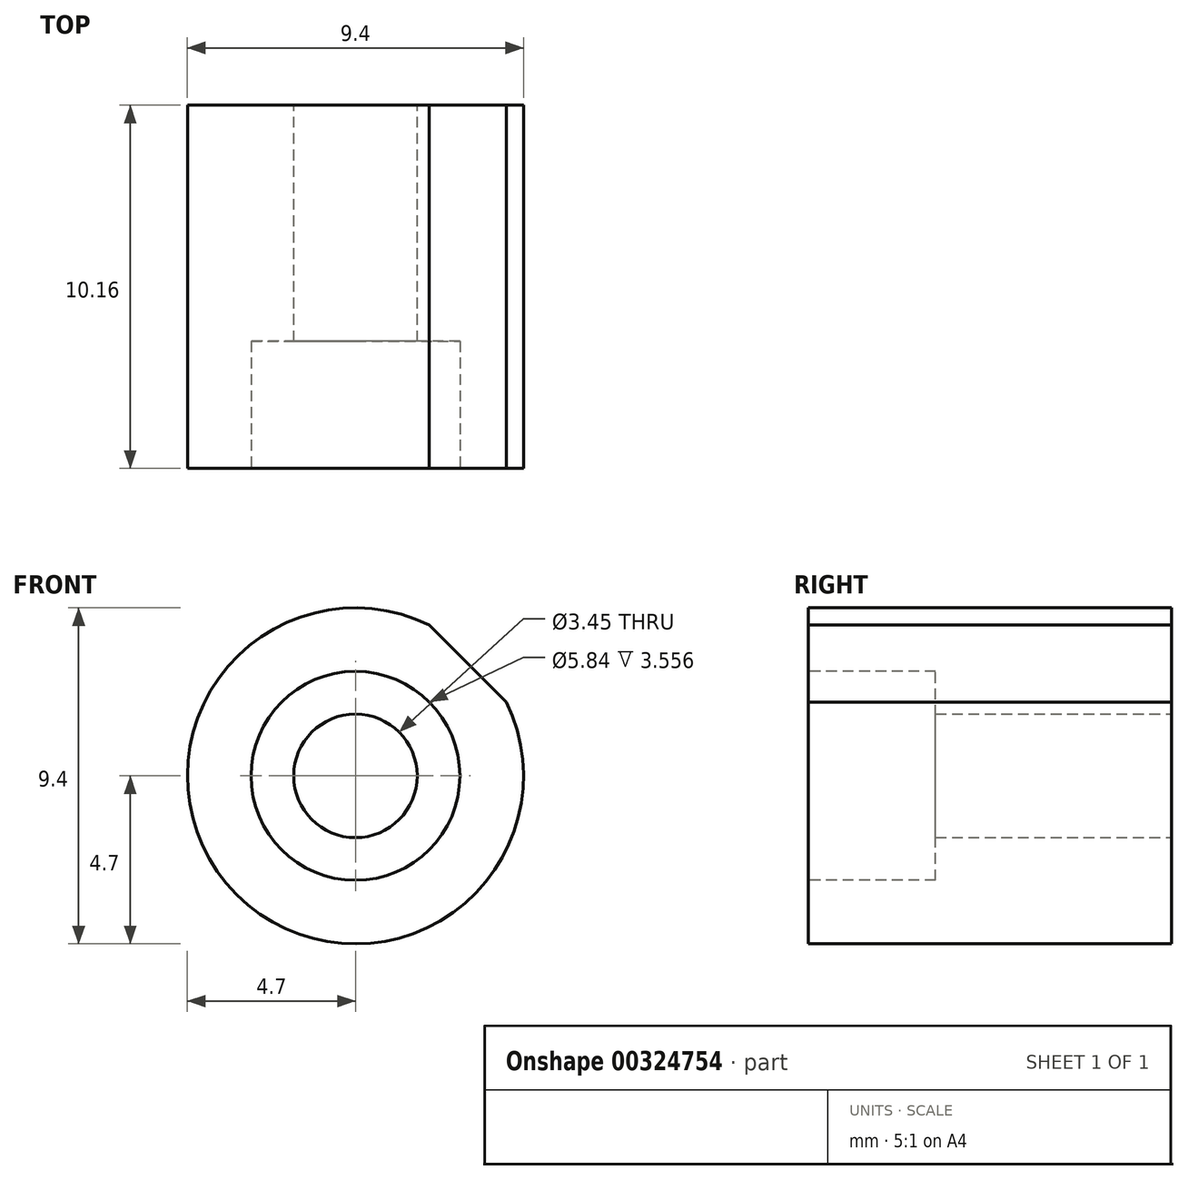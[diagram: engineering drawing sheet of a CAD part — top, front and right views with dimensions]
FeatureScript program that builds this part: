
annotation { "Feature Type Name" : "Feature", "Feature Type Description" : "" }
export const myFeature = defineFeature(function(context is Context, id is Id, definition is map)
    precondition{}
    {
        {
            var Q0;
            Q0=qCreatedBy(makeId("Front.planeOp"),FACE);
            var sketch = newSketch(context, id + "F0", { "sketchPlane" : qUnion([Q0])});
            skCircle(sketch, "E0", {"center": v(0, 0) * mm, "radius": 1.73 * mm});
            skCircle(sketch, "E1", {"center": v(0, 0) * mm, "radius": 4.7 * mm});
            skSolve(sketch);
        }
        {
            var Q0;
            Q0=makeQuery(id+"F0.imprint","IMPRINT",FACE,{"disambiguationData":[TD([[makeQuery(id+"F0.imprint","IMPRINT",EDGE,{"derivedFrom":sQuery(id+"F0.wireOp",EDGE,"E0")}),-1.0]])]});
            extrude(context, id + "F1", {"entities" : qUnion([Q0]), "depth" : 10.16 * mm, "offsetDistance" : 25.4 * mm});
        }
        {
            var Q0;
            Q0=makeQuery(id+"F1.opExtrude","CAP_FACE",FACE,{"disambiguationData":[OSD([sQuery(id+"F0.wireOp",EDGE,"E0"),sQuery(id+"F0.wireOp",EDGE,"E1")])],"isStart":false});
            var sketch = newSketch(context, id + "F2", { "sketchPlane" : qUnion([Q0])});
            skCircle(sketch, "E2", {"center": v(0, 0) * mm, "radius": 4.45 * mm, "construction": true});
            skLineSegment(sketch, "E3", {"start": v(1.12, 5.16) * mm, "end": v(6.29, 0) * mm});
            skArc(sketch, "E4", {"start": v(2.07, 4.22) * mm, "mid": v(3.32, 3.32) * mm, "end": v(4.22, 2.07) * mm});
            skSolve(sketch);
        }
        {
            var Q0;
            {var subQ0=sQuery(id+"F2.wireOp",EDGE,"E4");Q0=makeQuery(id+"F2.imprint","IMPRINT",FACE,{"disambiguationData":[TD([[makeQuery(id+"F2.imprint","IMPRINT",EDGE,{"derivedFrom":subQ0}),1.0]])]});}
            extrude(context, id + "F3", {"entities" : qUnion([Q0]), "operationType" : NewBodyOperationType.REMOVE, "endBound" : BoundingType.THROUGH_ALL, "oppositeDirection" : true, "depth" : 25.4 * mm, "offsetDistance" : 25.4 * mm});
        }
        {
            var Q0;
            Q0=makeQuery(id+"F1.opExtrude","CAP_FACE",FACE,{"disambiguationData":[OSD([sQuery(id+"F0.wireOp",EDGE,"E0"),sQuery(id+"F0.wireOp",EDGE,"E1")])],"isStart":false});
            var sketch = newSketch(context, id + "F4", { "sketchPlane" : qUnion([Q0])});
            skCircle(sketch, "E5", {"center": v(0, 0) * mm, "radius": 1.71 * mm});
            skCircle(sketch, "E6", {"center": v(0, 0) * mm, "radius": 2.92 * mm});
            skSolve(sketch);
        }
        {
            var Q0;
            Q0=makeQuery(id+"F4.imprint","IMPRINT",FACE,{"disambiguationData":[TD([[makeQuery(id+"F4.imprint","IMPRINT",EDGE,{"derivedFrom":sQuery(id+"F4.wireOp",EDGE,"E5")}),-1.0]])]});
            var Q1;
            Q1=makeQuery(id+"F4.imprint","IMPRINT",FACE,{"disambiguationData":[TD([[makeQuery(id+"F4.imprint","IMPRINT",EDGE,{"derivedFrom":sQuery(id+"F4.wireOp",EDGE,"E6")}),1.0]])]});
            extrude(context, id + "F5", {"entities" : qUnion([Q0, Q1]), "operationType" : NewBodyOperationType.REMOVE, "oppositeDirection" : true, "depth" : 3.56 * mm, "offsetDistance" : 25.4 * mm});
        }
    });
